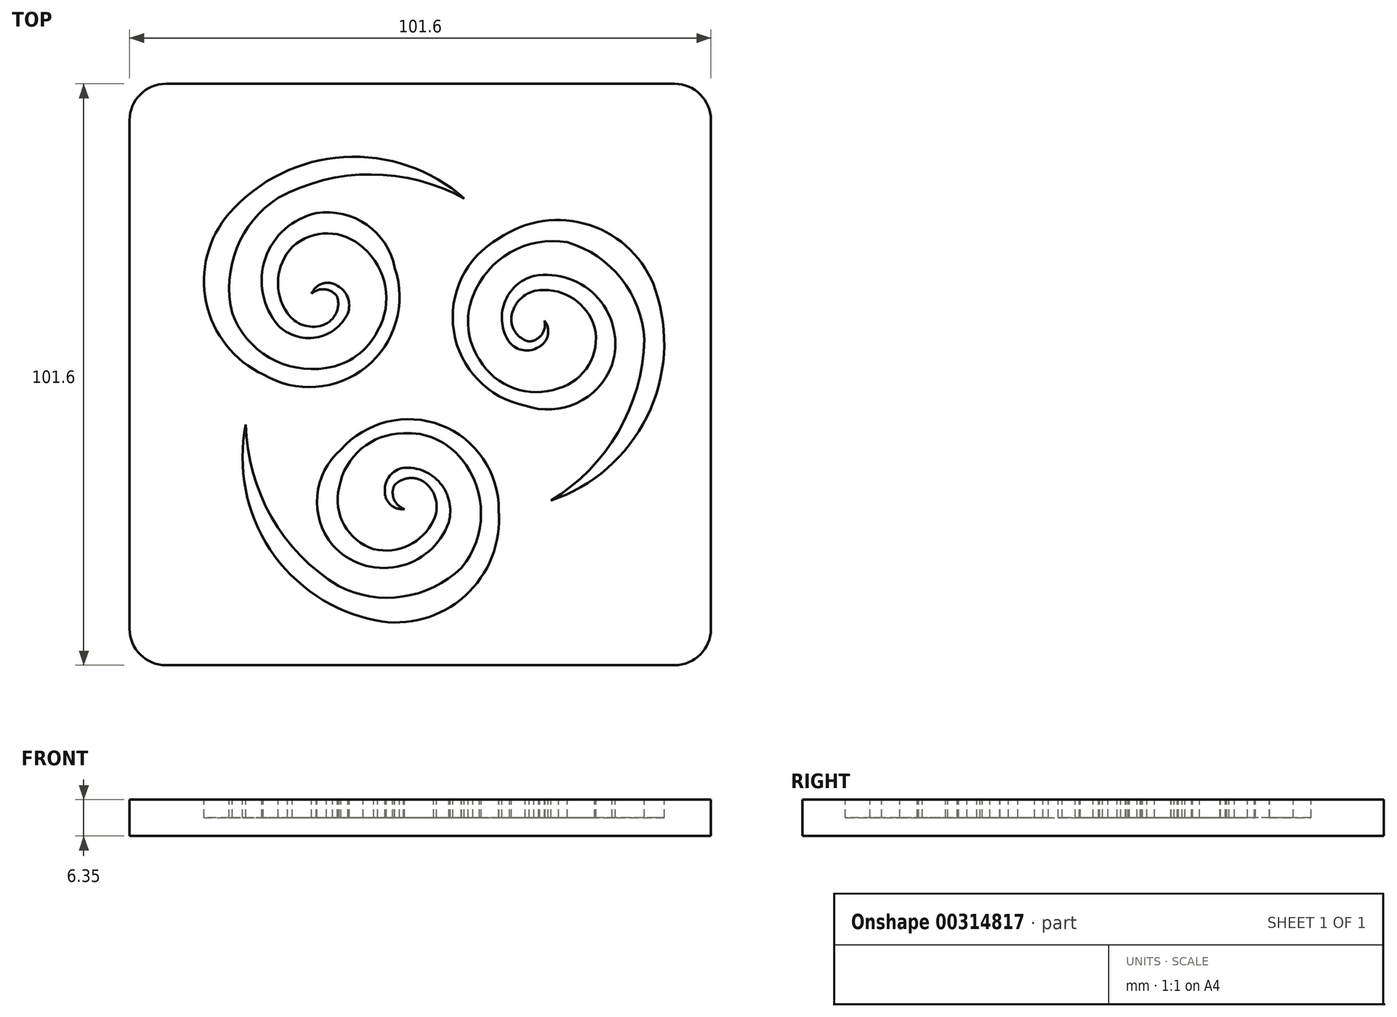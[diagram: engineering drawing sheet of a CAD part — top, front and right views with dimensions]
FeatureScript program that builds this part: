
annotation { "Feature Type Name" : "Feature", "Feature Type Description" : "" }
export const myFeature = defineFeature(function(context is Context, id is Id, definition is map)
    precondition{}
    {
        {
            var Q0;
            Q0=qCreatedBy(makeId("Top.planeOp"),FACE);
            var sketch = newSketch(context, id + "F0", { "sketchPlane" : qUnion([Q0])});
            skLineSegment(sketch, "E0.bottom", {"start": v(-44.45, 50.8) * mm, "end": v(44.45, 50.8) * mm});
            skLineSegment(sketch, "E0.top", {"start": v(-44.45, -50.8) * mm, "end": v(44.45, -50.8) * mm});
            skLineSegment(sketch, "E0.left", {"start": v(-50.8, 44.45) * mm, "end": v(-50.8, -44.45) * mm});
            skLineSegment(sketch, "E0.right", {"start": v(50.8, 44.45) * mm, "end": v(50.8, -44.45) * mm});
            skPoint(sketch, "E1.visualSharp", {"position": v(-50.8, 50.8) * mm});
            skArc(sketch, "E1.filletArc", {"start": v(-44.45, 50.8) * mm, "mid": v(-48.94, 48.94) * mm, "end": v(-50.8, 44.45) * mm});
            skPoint(sketch, "E2.visualSharp", {"position": v(50.8, 50.8) * mm});
            skArc(sketch, "E2.filletArc", {"start": v(50.8, 44.45) * mm, "mid": v(48.94, 48.94) * mm, "end": v(44.45, 50.8) * mm});
            skPoint(sketch, "E3.visualSharp", {"position": v(50.8, -50.8) * mm});
            skArc(sketch, "E3.filletArc", {"start": v(44.45, -50.8) * mm, "mid": v(48.94, -48.94) * mm, "end": v(50.8, -44.45) * mm});
            skPoint(sketch, "E4.visualSharp", {"position": v(-50.8, -50.8) * mm});
            skArc(sketch, "E4.filletArc", {"start": v(-50.8, -44.45) * mm, "mid": v(-48.94, -48.94) * mm, "end": v(-44.45, -50.8) * mm});
            skSolve(sketch);
        }
        {
            var Q0;
            Q0 = qSketchRegion(id + "F0", true);
            extrude(context, id + "F1", {"entities" : qUnion([Q0]), "depth" : 6.35 * mm});
        }
        {
            var Q0;
            Q0=makeQuery(id+"F1.opExtrude","CAP_FACE",FACE,{"disambiguationData":[OSD([sQuery(id+"F0.wireOp",EDGE,"E0.bottom"),sQuery(id+"F0.wireOp",EDGE,"E0.top"),sQuery(id+"F0.wireOp",EDGE,"E0.left"),sQuery(id+"F0.wireOp",EDGE,"E0.right"),sQuery(id+"F0.wireOp",EDGE,"E1.filletArc"),sQuery(id+"F0.wireOp",EDGE,"E2.filletArc"),sQuery(id+"F0.wireOp",EDGE,"E3.filletArc"),sQuery(id+"F0.wireOp",EDGE,"E4.filletArc")])],"isStart":false});
            var sketch = newSketch(context, id + "F2", { "sketchPlane" : qUnion([Q0])});
            skArc(sketch, "E5", {"start": v(7.66, 30.77) * mm, "mid": v(-13.4, 38) * mm, "end": v(-33.37, 28.19) * mm});
            skArc(sketch, "E6", {"start": v(-33.37, 28.19) * mm, "mid": v(-37.42, 12.61) * mm, "end": v(-27.43, 0) * mm});
            skArc(sketch, "E7", {"start": v(-27.43, 0) * mm, "mid": v(-9.47, 1.3) * mm, "end": v(-4.45, 18.58) * mm});
            skArc(sketch, "E8", {"start": v(-4.45, 18.58) * mm, "mid": v(-9.36, 26.18) * mm, "end": v(-18.17, 28.19) * mm});
            skArc(sketch, "E9", {"start": v(-18.17, 28.19) * mm, "mid": v(-27.07, 20.29) * mm, "end": v(-24.84, 8.6) * mm});
            skArc(sketch, "E10", {"start": v(-24.84, 8.6) * mm, "mid": v(-18.2, 6.47) * mm, "end": v(-12.66, 10.7) * mm});
            skArc(sketch, "E11", {"start": v(-12.66, 10.7) * mm, "mid": v(-12.68, 13.47) * mm, "end": v(-14.52, 15.54) * mm});
            skArc(sketch, "E12", {"start": v(-14.52, 15.54) * mm, "mid": v(-17.09, 15.88) * mm, "end": v(-19, 14.13) * mm});
            skArc(sketch, "E13", {"start": v(-14.52, 13.6) * mm, "mid": v(-16.64, 14.89) * mm, "end": v(-19, 14.13) * mm});
            skArc(sketch, "E14", {"start": v(-17.14, 8.6) * mm, "mid": v(-14.78, 10.55) * mm, "end": v(-14.52, 13.6) * mm});
            skArc(sketch, "E15", {"start": v(-23.19, 10.7) * mm, "mid": v(-20.51, 8.65) * mm, "end": v(-17.14, 8.6) * mm});
            skArc(sketch, "E16", {"start": v(-22.35, 22.28) * mm, "mid": v(-24.85, 16.64) * mm, "end": v(-23.19, 10.7) * mm});
            skArc(sketch, "E17", {"start": v(-10, 22.15) * mm, "mid": v(-16.15, 24.67) * mm, "end": v(-22.35, 22.28) * mm});
            skArc(sketch, "E18", {"start": v(-7.42, 7.68) * mm, "mid": v(-6.1, 15.38) * mm, "end": v(-10, 22.15) * mm});
            skArc(sketch, "E19", {"start": v(-16.41, 1.14) * mm, "mid": v(-11.1, 3.3) * mm, "end": v(-7.42, 7.68) * mm});
            skArc(sketch, "E20", {"start": v(-32.86, 10.7) * mm, "mid": v(-26.36, 2.96) * mm, "end": v(-16.41, 1.14) * mm});
            skArc(sketch, "E21", {"start": v(-24.85, 30.87) * mm, "mid": v(-32.08, 22.06) * mm, "end": v(-32.86, 10.7) * mm});
            skPoint(sketch, "E21.startSnap0", {"position": v(-24.85, 16.64) * mm});
            skArc(sketch, "E22", {"start": v(7.66, 30.77) * mm, "mid": v(-8.58, 34.97) * mm, "end": v(-24.85, 30.87) * mm});
            skArc(sketch, "E23.1.0", {"start": v(-2.94, -10.27) * mm, "mid": v(-10.27, -12.97) * mm, "end": v(-14.18, -19.74) * mm});
            skArc(sketch, "E23.1.1", {"start": v(-30.48, -8.75) * mm, "mid": v(-26, -24.92) * mm, "end": v(-14.3, -36.95) * mm});
            skArc(sketch, "E23.1.2", {"start": v(7.17, -33.81) * mm, "mid": v(10.62, -24.3) * mm, "end": v(7.22, -14.79) * mm});
            skPoint(sketch, "E23.1.3", {"position": v(-1.99, -29.84) * mm});
            skArc(sketch, "E23.1.4", {"start": v(-14.18, -19.74) * mm, "mid": v(-13.29, -26.32) * mm, "end": v(-8.12, -30.5) * mm});
            skArc(sketch, "E23.1.5", {"start": v(1.12, -19.14) * mm, "mid": v(-1.75, -18.08) * mm, "end": v(-4.52, -19.38) * mm});
            skArc(sketch, "E23.1.6", {"start": v(7.22, -14.79) * mm, "mid": v(2.7, -11.27) * mm, "end": v(-2.94, -10.27) * mm});
            skArc(sketch, "E23.1.7", {"start": v(2.33, -25.43) * mm, "mid": v(2.77, -22.09) * mm, "end": v(1.12, -19.14) * mm});
            skArc(sketch, "E23.1.8", {"start": v(-14.3, -36.95) * mm, "mid": v(-3.07, -38.81) * mm, "end": v(7.17, -33.81) * mm});
            skArc(sketch, "E23.1.9", {"start": v(-8.12, -30.5) * mm, "mid": v(-1.99, -29.84) * mm, "end": v(2.33, -25.43) * mm});
            skArc(sketch, "E23.1.10", {"start": v(-30.48, -8.75) * mm, "mid": v(-26.22, -30.6) * mm, "end": v(-7.72, -43) * mm});
            skArc(sketch, "E23.1.11", {"start": v(-2.93, -16.32) * mm, "mid": v(-5.33, -17.71) * mm, "end": v(-6.2, -20.34) * mm});
            skArc(sketch, "E23.1.12", {"start": v(4.98, -25.81) * mm, "mid": v(3.5, -19) * mm, "end": v(-2.93, -16.32) * mm});
            skArc(sketch, "E23.1.13", {"start": v(-7.72, -43) * mm, "mid": v(7.79, -38.71) * mm, "end": v(13.71, -23.75) * mm});
            skArc(sketch, "E23.1.14", {"start": v(13.71, -23.75) * mm, "mid": v(3.61, -8.85) * mm, "end": v(-13.87, -13.14) * mm});
            skArc(sketch, "E23.1.15", {"start": v(-15.33, -29.83) * mm, "mid": v(-4.03, -33.6) * mm, "end": v(4.98, -25.81) * mm});
            skArc(sketch, "E23.1.16", {"start": v(-13.87, -13.14) * mm, "mid": v(-18, -21.2) * mm, "end": v(-15.33, -29.83) * mm});
            skArc(sketch, "E23.1.17", {"start": v(-4.52, -19.38) * mm, "mid": v(-4.57, -21.85) * mm, "end": v(-2.74, -23.51) * mm});
            skArc(sketch, "E23.1.18", {"start": v(-6.2, -20.34) * mm, "mid": v(-5.2, -22.74) * mm, "end": v(-2.74, -23.51) * mm});
            skArc(sketch, "E23.2.0", {"start": v(10.36, 2.6) * mm, "mid": v(16.37, -2.4) * mm, "end": v(24.18, -2.41) * mm});
            skArc(sketch, "E23.2.1", {"start": v(22.82, -22.02) * mm, "mid": v(34.58, -10.06) * mm, "end": v(39.16, 6.08) * mm});
            skArc(sketch, "E23.2.2", {"start": v(25.7, 23.11) * mm, "mid": v(15.74, 21.35) * mm, "end": v(9.2, 13.64) * mm});
            skPoint(sketch, "E23.2.3", {"position": v(26.84, 13.2) * mm});
            skArc(sketch, "E23.2.4", {"start": v(24.18, -2.41) * mm, "mid": v(29.44, 1.65) * mm, "end": v(30.48, 8.22) * mm});
            skArc(sketch, "E23.2.5", {"start": v(16.02, 10.55) * mm, "mid": v(16.53, 7.53) * mm, "end": v(19.04, 5.77) * mm});
            skArc(sketch, "E23.2.6", {"start": v(9.2, 13.64) * mm, "mid": v(8.4, 7.97) * mm, "end": v(10.36, 2.6) * mm});
            skArc(sketch, "E23.2.7", {"start": v(20.86, 14.73) * mm, "mid": v(17.74, 13.44) * mm, "end": v(16.02, 10.55) * mm});
            skArc(sketch, "E23.2.8", {"start": v(39.16, 6.08) * mm, "mid": v(35.15, 16.75) * mm, "end": v(25.7, 23.11) * mm});
            skArc(sketch, "E23.2.9", {"start": v(30.48, 8.22) * mm, "mid": v(26.84, 13.2) * mm, "end": v(20.86, 14.73) * mm});
            skArc(sketch, "E23.2.10", {"start": v(22.82, -22.02) * mm, "mid": v(39.6, -7.4) * mm, "end": v(41.1, 14.8) * mm});
            skArc(sketch, "E23.2.11", {"start": v(15.6, 5.62) * mm, "mid": v(18, 4.25) * mm, "end": v(20.72, 4.8) * mm});
            skArc(sketch, "E23.2.12", {"start": v(19.87, 17.22) * mm, "mid": v(14.7, 12.53) * mm, "end": v(15.6, 5.62) * mm});
            skArc(sketch, "E23.2.13", {"start": v(41.1, 14.8) * mm, "mid": v(29.63, 26.1) * mm, "end": v(13.71, 23.75) * mm});
            skArc(sketch, "E23.2.14", {"start": v(13.71, 23.75) * mm, "mid": v(5.86, 7.55) * mm, "end": v(18.32, -5.44) * mm});
            skArc(sketch, "E23.2.15", {"start": v(33.5, 1.64) * mm, "mid": v(31.1, 13.3) * mm, "end": v(19.87, 17.22) * mm});
            skArc(sketch, "E23.2.16", {"start": v(18.32, -5.44) * mm, "mid": v(27.35, -4.99) * mm, "end": v(33.5, 1.64) * mm});
            skArc(sketch, "E23.2.17", {"start": v(19.04, 5.77) * mm, "mid": v(21.21, 6.96) * mm, "end": v(21.73, 9.39) * mm});
            skArc(sketch, "E23.2.18", {"start": v(20.72, 4.8) * mm, "mid": v(22.3, 6.86) * mm, "end": v(21.73, 9.39) * mm});
            skPoint(sketch, "E23.center", {"position": v(0, 0) * mm});
            skSolve(sketch);
        }
        {
            var Q0;
            Q0 = qSketchRegion(id + "F2", true);
            extrude(context, id + "F3", {"entities" : qUnion([Q0]), "operationType" : NewBodyOperationType.REMOVE, "oppositeDirection" : true, "depth" : 3.17 * mm});
        }
    });
